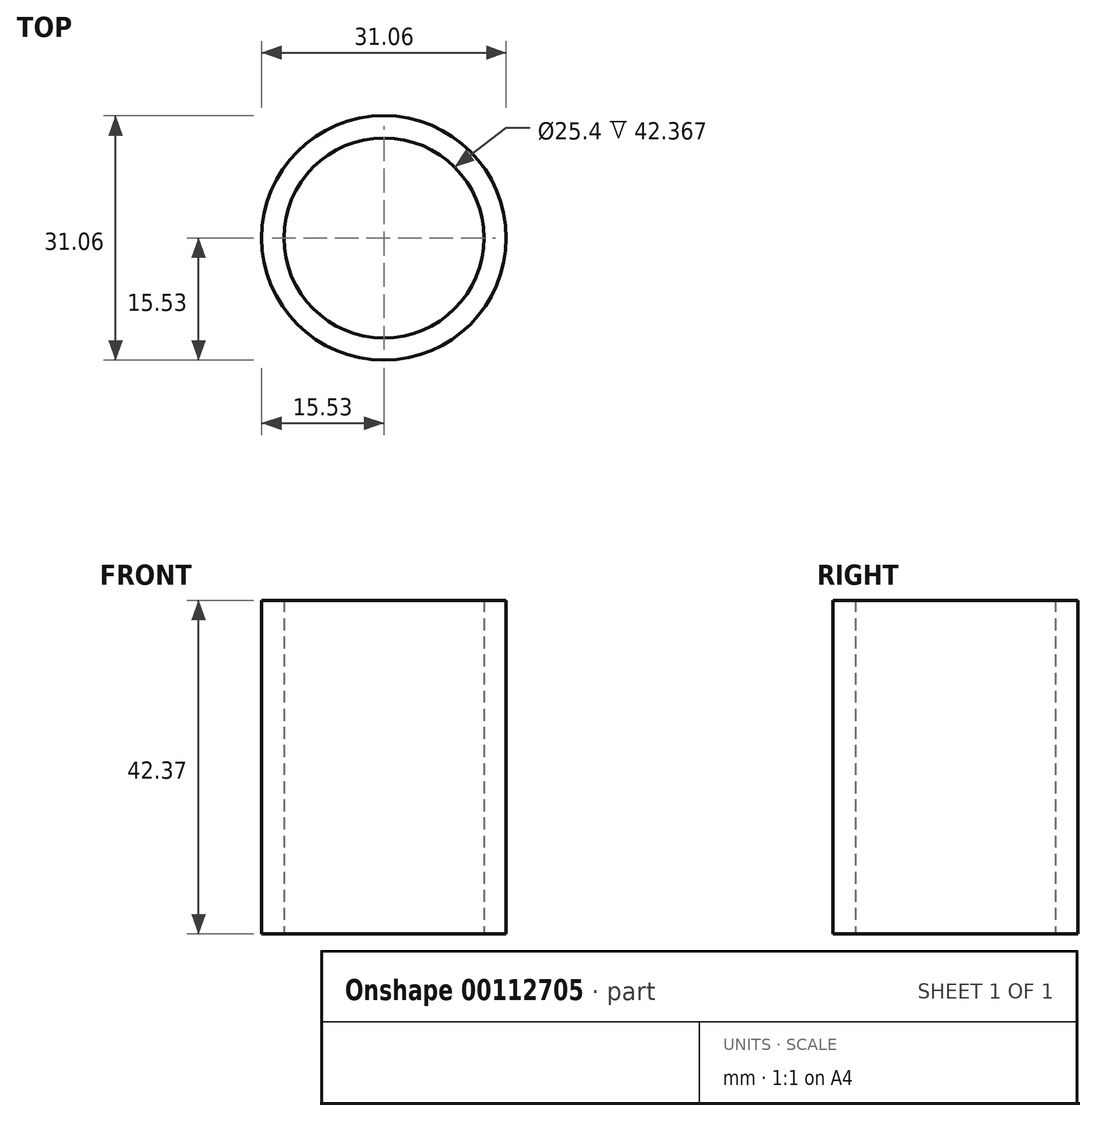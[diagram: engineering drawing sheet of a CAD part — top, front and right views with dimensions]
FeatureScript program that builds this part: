
annotation { "Feature Type Name" : "Feature", "Feature Type Description" : "" }
export const myFeature = defineFeature(function(context is Context, id is Id, definition is map)
    precondition{}
    {
        {
            var Q0;
            Q0=qCreatedBy(makeId("Top.planeOp"),FACE);
            var sketch = newSketch(context, id + "F0", { "sketchPlane" : qUnion([Q0])});
            skCircle(sketch, "E0", {"center": v(0, 0) * mm, "radius": 15.53 * mm});
            skCircle(sketch, "E1", {"center": v(0, 0) * mm, "radius": 12.7 * mm});
            skSolve(sketch);
        }
        {
            var Q0;
            Q0=qSketchRegion(id+"F0",true);
            extrude(context, id + "F1", {"entities" : qUnion([Q0]), "depth" : 42.37 * mm});
        }
    });
